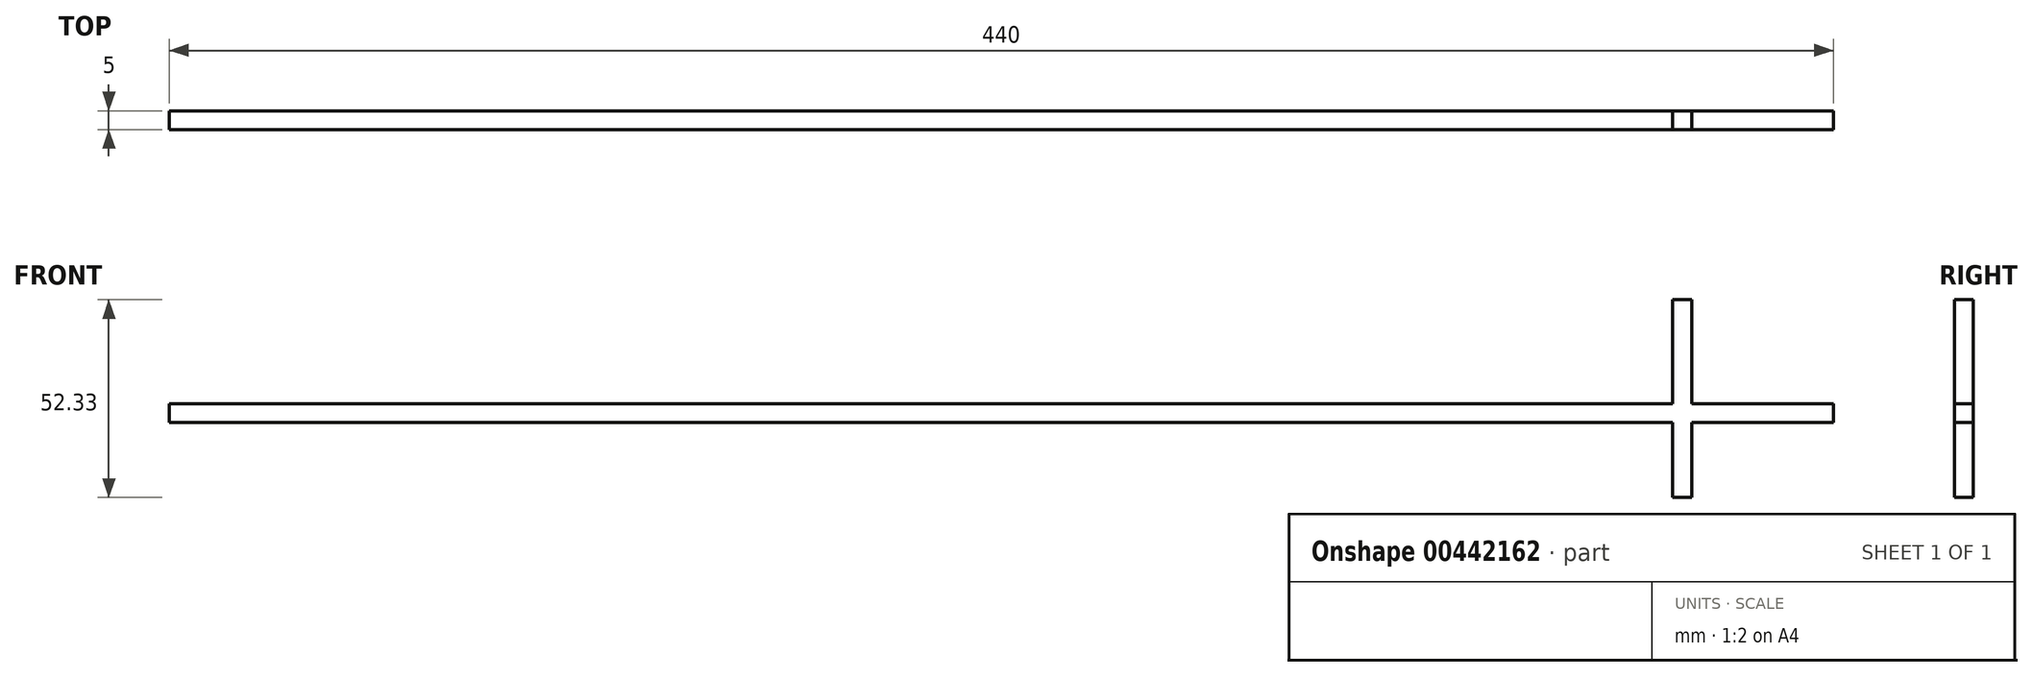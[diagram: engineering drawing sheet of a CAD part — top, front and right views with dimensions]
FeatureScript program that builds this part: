
annotation { "Feature Type Name" : "Feature", "Feature Type Description" : "" }
export const myFeature = defineFeature(function(context is Context, id is Id, definition is map)
    precondition{}
    {
        {
            var Q0;
            Q0=qCreatedBy(makeId("Front.planeOp"),FACE);
            var sketch = newSketch(context, id + "F0", { "sketchPlane" : qUnion([Q0])});
            skLineSegment(sketch, "E0", {"start": v(-234.06, 12.13) * mm, "end": v(-194.06, 12.13) * mm});
            skLineSegment(sketch, "E1", {"start": v(-194.06, 12.13) * mm, "end": v(-154.06, 12.13) * mm});
            skLineSegment(sketch, "E2", {"start": v(-154.06, 12.13) * mm, "end": v(-114.06, 12.13) * mm});
            skLineSegment(sketch, "E3", {"start": v(-114.06, 12.13) * mm, "end": v(-74.06, 12.13) * mm});
            skLineSegment(sketch, "E4", {"start": v(-74.06, 12.13) * mm, "end": v(-34.06, 12.13) * mm});
            skLineSegment(sketch, "E5", {"start": v(-34.06, 12.13) * mm, "end": v(5.94, 12.13) * mm});
            skLineSegment(sketch, "E6", {"start": v(5.94, 12.13) * mm, "end": v(45.94, 12.13) * mm});
            skLineSegment(sketch, "E7", {"start": v(45.94, 12.13) * mm, "end": v(85.94, 12.13) * mm});
            skLineSegment(sketch, "E8", {"start": v(85.94, 12.13) * mm, "end": v(125.94, 12.13) * mm});
            skLineSegment(sketch, "E9", {"start": v(125.94, 12.13) * mm, "end": v(165.94, 12.13) * mm});
            skLineSegment(sketch, "E10", {"start": v(165.94, 12.13) * mm, "end": v(205.94, 12.13) * mm});
            skLineSegment(sketch, "E11", {"start": v(-194.06, 12.13) * mm, "end": v(-194.06, 42.13) * mm});
            skLineSegment(sketch, "E12", {"start": v(-154.06, 12.13) * mm, "end": v(-154.06, 32.13) * mm});
            skLineSegment(sketch, "E13", {"start": v(-234.06, 12.13) * mm, "end": v(-194.06, 42.13) * mm});
            skLineSegment(sketch, "E14", {"start": v(-194.06, 42.13) * mm, "end": v(-154.06, 32.13) * mm});
            skLineSegment(sketch, "E15", {"start": v(-194.06, 12.13) * mm, "end": v(-154.06, 32.13) * mm});
            skLineSegment(sketch, "E16", {"start": v(-154.06, 32.13) * mm, "end": v(-154.06, 52.13) * mm});
            skLineSegment(sketch, "E17", {"start": v(-194.06, 42.13) * mm, "end": v(-154.06, 52.13) * mm});
            skLineSegment(sketch, "E18", {"start": v(-114.06, 12.13) * mm, "end": v(-114.06, 42.13) * mm});
            skLineSegment(sketch, "E19", {"start": v(-114.06, 42.13) * mm, "end": v(-114.06, 62.13) * mm});
            skLineSegment(sketch, "E20", {"start": v(-154.06, 52.13) * mm, "end": v(-114.06, 62.13) * mm});
            skLineSegment(sketch, "E21", {"start": v(-114.06, 42.13) * mm, "end": v(-154.06, 32.13) * mm});
            skLineSegment(sketch, "E22", {"start": v(-74.06, 12.13) * mm, "end": v(-74.06, 52.13) * mm});
            skLineSegment(sketch, "E23", {"start": v(-74.06, 52.13) * mm, "end": v(-74.06, 72.13) * mm});
            skLineSegment(sketch, "E24", {"start": v(-114.06, 62.13) * mm, "end": v(-74.06, 72.13) * mm});
            skLineSegment(sketch, "E25", {"start": v(-74.06, 52.13) * mm, "end": v(-114.06, 42.13) * mm});
            skLineSegment(sketch, "E26", {"start": v(-154.06, 52.13) * mm, "end": v(-114.06, 42.13) * mm});
            skLineSegment(sketch, "E27", {"start": v(-114.06, 62.13) * mm, "end": v(-74.06, 52.13) * mm});
            skLineSegment(sketch, "E28", {"start": v(-34.06, 12.13) * mm, "end": v(-34.06, 52.13) * mm});
            skLineSegment(sketch, "E29", {"start": v(-34.06, 52.13) * mm, "end": v(-34.06, 82.13) * mm});
            skLineSegment(sketch, "E30", {"start": v(-34.06, 82.13) * mm, "end": v(-74.06, 72.13) * mm});
            skLineSegment(sketch, "E31", {"start": v(-74.06, 52.13) * mm, "end": v(-34.06, 52.13) * mm});
            skLineSegment(sketch, "E32", {"start": v(-74.06, 72.13) * mm, "end": v(-34.06, 52.13) * mm});
            skLineSegment(sketch, "E33", {"start": v(5.94, 12.13) * mm, "end": v(5.94, 52.13) * mm});
            skLineSegment(sketch, "E34", {"start": v(5.94, 52.13) * mm, "end": v(5.94, 82.13) * mm});
            skLineSegment(sketch, "E35", {"start": v(5.94, 82.13) * mm, "end": v(-34.06, 82.13) * mm});
            skLineSegment(sketch, "E36", {"start": v(-34.06, 82.13) * mm, "end": v(5.94, 52.13) * mm});
            skLineSegment(sketch, "E37", {"start": v(5.94, 82.13) * mm, "end": v(-34.06, 52.13) * mm});
            skLineSegment(sketch, "E38", {"start": v(-34.06, 52.13) * mm, "end": v(5.94, 52.13) * mm});
            skLineSegment(sketch, "E39", {"start": v(45.94, 12.13) * mm, "end": v(45.94, 52.13) * mm});
            skLineSegment(sketch, "E40", {"start": v(45.94, 52.13) * mm, "end": v(45.94, 72.13) * mm});
            skLineSegment(sketch, "E41", {"start": v(45.94, 72.13) * mm, "end": v(5.94, 82.13) * mm});
            skLineSegment(sketch, "E42", {"start": v(5.94, 52.13) * mm, "end": v(45.94, 52.13) * mm});
            skLineSegment(sketch, "E43", {"start": v(45.94, 72.13) * mm, "end": v(5.94, 52.13) * mm});
            skLineSegment(sketch, "E44", {"start": v(85.94, 12.13) * mm, "end": v(85.94, 42.13) * mm});
            skLineSegment(sketch, "E45", {"start": v(85.94, 42.13) * mm, "end": v(85.94, 62.13) * mm});
            skLineSegment(sketch, "E46", {"start": v(45.94, 72.13) * mm, "end": v(85.94, 62.13) * mm});
            skLineSegment(sketch, "E47", {"start": v(45.94, 52.13) * mm, "end": v(85.94, 42.13) * mm});
            skLineSegment(sketch, "E48", {"start": v(85.94, 62.13) * mm, "end": v(45.94, 52.13) * mm});
            skLineSegment(sketch, "E49", {"start": v(125.94, 12.13) * mm, "end": v(125.94, 32.13) * mm});
            skLineSegment(sketch, "E50", {"start": v(125.94, 32.13) * mm, "end": v(125.94, 52.13) * mm});
            skLineSegment(sketch, "E51", {"start": v(85.94, 62.13) * mm, "end": v(125.94, 52.13) * mm});
            skLineSegment(sketch, "E52", {"start": v(125.94, 32.13) * mm, "end": v(85.94, 42.13) * mm});
            skLineSegment(sketch, "E53", {"start": v(125.94, 52.13) * mm, "end": v(85.94, 42.13) * mm});
            skLineSegment(sketch, "E54", {"start": v(165.94, 12.13) * mm, "end": v(165.94, 42.13) * mm});
            skLineSegment(sketch, "E55", {"start": v(165.94, 42.13) * mm, "end": v(125.94, 52.13) * mm});
            skLineSegment(sketch, "E56", {"start": v(165.94, 42.13) * mm, "end": v(125.94, 32.13) * mm});
            skLineSegment(sketch, "E57", {"start": v(125.94, 32.13) * mm, "end": v(165.94, 12.13) * mm});
            skLineSegment(sketch, "E58", {"start": v(165.94, 42.13) * mm, "end": v(205.94, 12.13) * mm});
            skLineSegment(sketch, "E59", {"start": v(-194.06, 12.13) * mm, "end": v(-194.06, -10.37) * mm});
            skLineSegment(sketch, "E60", {"start": v(165.94, 12.13) * mm, "end": v(165.94, -10.37) * mm});
            skLineSegment(sketch, "E61", {"start": v(-234.06, 12.13) * mm, "end": v(-194.06, -10.37) * mm});
            skLineSegment(sketch, "E62", {"start": v(205.94, 12.13) * mm, "end": v(165.94, -10.37) * mm});
            skLineSegment(sketch, "E63", {"start": v(-114.06, 12.13) * mm, "end": v(-114.06, -15.37) * mm});
            skLineSegment(sketch, "E64", {"start": v(85.94, 12.13) * mm, "end": v(85.94, -15.37) * mm});
            skLineSegment(sketch, "E65", {"start": v(-154.06, 12.13) * mm, "end": v(-154.06, -12.87) * mm});
            skLineSegment(sketch, "E66", {"start": v(125.94, 12.13) * mm, "end": v(125.94, -12.87) * mm});
            skLineSegment(sketch, "E67", {"start": v(-194.06, -10.37) * mm, "end": v(-154.06, -12.87) * mm});
            skLineSegment(sketch, "E68", {"start": v(-194.06, 12.13) * mm, "end": v(-114.06, -15.37) * mm});
            skLineSegment(sketch, "E69", {"start": v(-114.06, 12.13) * mm, "end": v(-194.06, -10.37) * mm});
            skLineSegment(sketch, "E70", {"start": v(85.94, -15.37) * mm, "end": v(125.94, -12.87) * mm});
            skLineSegment(sketch, "E71", {"start": v(125.94, -12.87) * mm, "end": v(165.94, -10.37) * mm});
            skLineSegment(sketch, "E72", {"start": v(165.94, 12.13) * mm, "end": v(85.94, -15.37) * mm});
            skLineSegment(sketch, "E73", {"start": v(85.94, 12.13) * mm, "end": v(165.94, -10.37) * mm});
            skLineSegment(sketch, "E74", {"start": v(-34.06, 12.13) * mm, "end": v(-34.06, -17.87) * mm});
            skLineSegment(sketch, "E75", {"start": v(5.94, 12.13) * mm, "end": v(5.94, -17.87) * mm});
            skLineSegment(sketch, "E76", {"start": v(-34.06, -17.87) * mm, "end": v(5.94, -17.87) * mm});
            skLineSegment(sketch, "E77", {"start": v(-34.06, 12.13) * mm, "end": v(5.94, -17.87) * mm});
            skLineSegment(sketch, "E78", {"start": v(5.94, 12.13) * mm, "end": v(-34.06, -17.87) * mm});
            skLineSegment(sketch, "E79", {"start": v(-114.06, 12.13) * mm, "end": v(-34.06, -17.87) * mm});
            skLineSegment(sketch, "E80", {"start": v(85.94, 12.13) * mm, "end": v(5.94, -17.87) * mm});
            skLineSegment(sketch, "E81", {"start": v(45.94, 12.13) * mm, "end": v(45.94, -17.87) * mm});
            skLineSegment(sketch, "E82", {"start": v(-74.06, 12.13) * mm, "end": v(-74.06, -17.87) * mm});
            skLineSegment(sketch, "E83", {"start": v(-114.06, -15.37) * mm, "end": v(-74.06, -17.87) * mm});
            skLineSegment(sketch, "E84", {"start": v(-34.06, -17.87) * mm, "end": v(-74.06, -17.87) * mm});
            skLineSegment(sketch, "E85", {"start": v(45.94, -17.87) * mm, "end": v(85.94, -15.37) * mm});
            skLineSegment(sketch, "E86", {"start": v(45.94, -17.87) * mm, "end": v(5.94, -17.87) * mm});
            skLineSegment(sketch, "E87", {"start": v(-154.06, -12.87) * mm, "end": v(-114.06, -15.37) * mm});
            skSolve(sketch);
        }
        {
            var Q0;
            Q0=sQuery(id+"F0.wireOp",VERTEX,"E62.start");
            var Q1;
            Q1=sQuery(id+"F0.wireOp",EDGE,"E10");
            cPlane(context, id + "F1", {"entities" : qUnion([Q0, Q1]), "cplaneType" : CPlaneType.LINE_POINT, "offset" : 25.4 * mm, "width" : 152.4 * mm, "height" : 152.4 * mm});
        }
        {
            var Q0;
            Q0=qCreatedBy(id+"F1.planeOp",FACE);
            var sketch = newSketch(context, id + "F2", { "sketchPlane" : qUnion([Q0])});
            skPoint(sketch, "E88.0", {"position": v(0, 12.13) * mm});
            skLineSegment(sketch, "E89.bottom", {"start": v(2.5, 9.63) * mm, "end": v(-2.5, 9.63) * mm});
            skLineSegment(sketch, "E89.top", {"start": v(2.5, 14.63) * mm, "end": v(-2.5, 14.63) * mm});
            skLineSegment(sketch, "E89.left", {"start": v(2.5, 9.63) * mm, "end": v(2.5, 14.63) * mm});
            skLineSegment(sketch, "E89.right", {"start": v(-2.5, 9.63) * mm, "end": v(-2.5, 14.63) * mm});
            skSolve(sketch);
        }
        {
            var Q0;
            Q0=sQuery(id+"F0.wireOp",VERTEX,"E0.start");
            var Q1;
            Q1=sQuery(id+"F0.wireOp",EDGE,"E0");
            cPlane(context, id + "F3", {"entities" : qUnion([Q0, Q1]), "cplaneType" : CPlaneType.LINE_POINT, "offset" : 25.4 * mm, "width" : 152.4 * mm, "height" : 152.4 * mm});
        }
        {
            var Q0;
            Q0 = qSketchRegion(id + "F2", true);
            var Q1;
            Q1=qCreatedBy(id+"F3.planeOp",FACE);
            extrude(context, id + "F4", {"entities" : qUnion([Q0]), "endBound" : BoundingType.UP_TO_SURFACE, "oppositeDirection" : true, "endBoundEntityFace" : qUnion([Q1]), "depth" : 25.4 * mm});
        }
        {
            var Q0;
            Q0=sQuery(id+"F0.wireOp",VERTEX,"E56.start");
            var Q1;
            Q1=sQuery(id+"F0.wireOp",EDGE,"E54");
            cPlane(context, id + "F5", {"entities" : qUnion([Q0, Q1]), "cplaneType" : CPlaneType.LINE_POINT, "offset" : 25.4 * mm, "width" : 152.4 * mm, "height" : 152.4 * mm});
        }
        {
            var Q0;
            Q0=sQuery(id+"F0.wireOp",VERTEX,"E60.end");
            var Q1;
            Q1=sQuery(id+"F0.wireOp",EDGE,"E60");
            cPlane(context, id + "F6", {"entities" : qUnion([Q0, Q1]), "cplaneType" : CPlaneType.LINE_POINT, "offset" : 25.4 * mm, "width" : 152.4 * mm, "height" : 152.4 * mm});
        }
        {
            var Q0;
            Q0=qCreatedBy(id+"F5.planeOp",FACE);
            var sketch = newSketch(context, id + "F7", { "sketchPlane" : qUnion([Q0])});
            skPoint(sketch, "E90.0", {"position": v(165.94, 0) * mm});
            skLineSegment(sketch, "E91.bottom", {"start": v(163.44, -2.5) * mm, "end": v(168.44, -2.5) * mm});
            skLineSegment(sketch, "E91.top", {"start": v(163.44, 2.5) * mm, "end": v(168.44, 2.5) * mm});
            skLineSegment(sketch, "E91.left", {"start": v(163.44, -2.5) * mm, "end": v(163.44, 2.5) * mm});
            skLineSegment(sketch, "E91.right", {"start": v(168.44, -2.5) * mm, "end": v(168.44, 2.5) * mm});
            skSolve(sketch);
        }
        {
            var Q0;
            Q0 = qSketchRegion(id + "F7", true);
            extrude(context, id + "F8", {"entities" : qUnion([Q0]), "operationType" : NewBodyOperationType.ADD, "oppositeDirection" : true, "depth" : 52.32 * mm});
        }
    });
